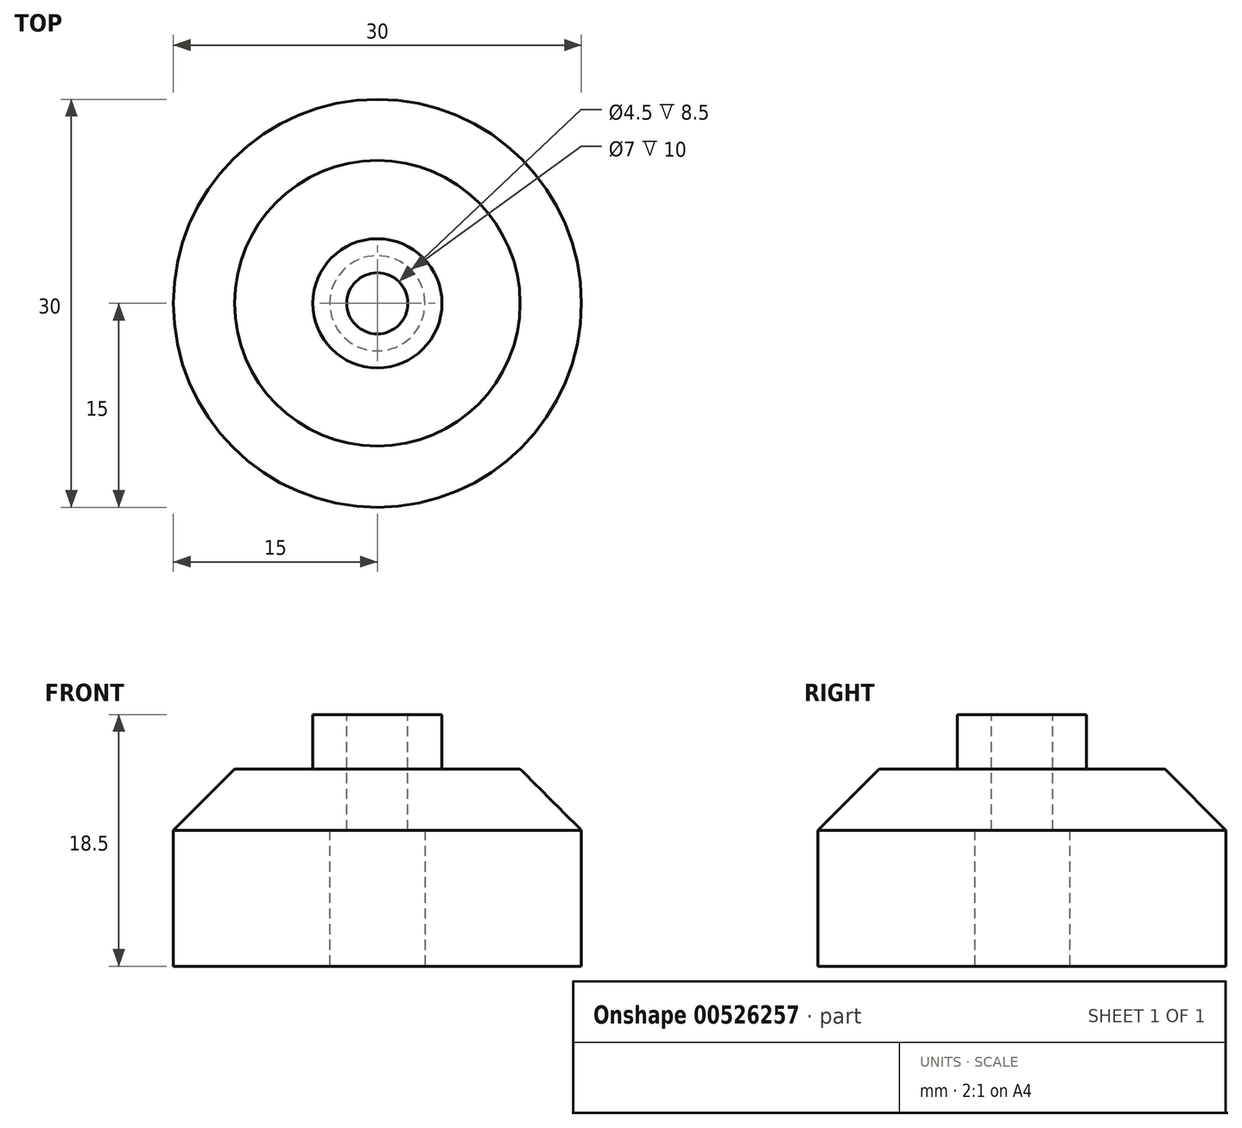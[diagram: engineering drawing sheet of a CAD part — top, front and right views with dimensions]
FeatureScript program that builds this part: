
annotation { "Feature Type Name" : "Feature", "Feature Type Description" : "" }
export const myFeature = defineFeature(function(context is Context, id is Id, definition is map)
    precondition{}
    {
        {
            var Q0;
            Q0=qCreatedBy(makeId("Top.planeOp"),FACE);
            var sketch = newSketch(context, id + "F0", { "sketchPlane" : qUnion([Q0])});
            skCircle(sketch, "E0", {"center": v(0, 0) * mm, "radius": 15 * mm});
            skSolve(sketch);
        }
        {
            var Q0;
            Q0=makeQuery(id+"F0.imprint","IMPRINT",FACE,{"disambiguationData":[TD([[makeQuery(id+"F0.imprint","IMPRINT",EDGE,{"derivedFrom":sQuery(id+"F0.wireOp",EDGE,"E0")}),1.0]])]});
            var Q1;
            Q1=sQuery(id+"F0.wireOp",EDGE,"E0");
            extrude(context, id + "F1", {"entities" : qUnion([Q0]), "surfaceEntities" : qUnion([Q1]), "depth" : 10 * mm, "offsetDistance" : 25.4 * mm});
        }
        {
            var Q0;
            Q0=makeQuery(id+"F1.opExtrude","CAP_FACE",FACE,{"disambiguationData":[OSD([sQuery(id+"F0.wireOp",EDGE,"E0")])],"isStart":false});
            var sketch = newSketch(context, id + "F2", { "sketchPlane" : qUnion([Q0])});
            skSolve(sketch);
        }
        {
            var Q0;
            Q0=makeQuery(id+"F2.imprint","IMPRINT",FACE,{"disambiguationData":[TD([[makeQuery(id+"F2.imprint","IMPRINT",EDGE,{"derivedFrom":makeQuery(id+"F1.opExtrude","CAP_EDGE",EDGE,{"disambiguationData":[OSD([sQuery(id+"F0.wireOp",EDGE,"E0")])],"isStart":false})}),1.0]])]});
            extrude(context, id + "F3", {"entities" : qUnion([Q0]), "operationType" : NewBodyOperationType.ADD, "depth" : 4.5 * mm, "offsetDistance" : 25.4 * mm});
        }
        {
            var Q0;
            Q0=makeQuery(id+"F3.opExtrude","CAP_EDGE",EDGE,{"disambiguationData":[OSD([sQuery(id+"F0.wireOp",EDGE,"E0")])],"isStart":false});
            chamfer(context, id + "F4", {"entities" : qUnion([Q0]), "chamferType" : ChamferType.OFFSET_ANGLE, "width" : 4.5 * mm, "oppositeDirection" : false, "angle" : 45 * degree, "tangentPropagation" : true});
        }
        {
            var Q0;
            Q0=makeQuery(id+"F3.opExtrude","CAP_FACE",FACE,{"disambiguationData":[OSD([sQuery(id+"F0.wireOp",EDGE,"E0")])],"isStart":false});
            var sketch = newSketch(context, id + "F5", { "sketchPlane" : qUnion([Q0])});
            skCircle(sketch, "E1", {"center": v(0, 0) * mm, "radius": 2.25 * mm});
            skSolve(sketch);
        }
        {
            var Q0;
            Q0=makeQuery(id+"F5.imprint","IMPRINT",FACE,{"disambiguationData":[TD([[makeQuery(id+"F5.imprint","IMPRINT",EDGE,{"derivedFrom":sQuery(id+"F5.wireOp",EDGE,"E1")}),1.0]])]});
            extrude(context, id + "F6", {"entities" : qUnion([Q0]), "operationType" : NewBodyOperationType.REMOVE, "oppositeDirection" : true, "depth" : 4.5 * mm, "offsetDistance" : 25.4 * mm});
        }
        {
            var Q0;
            Q0=makeQuery(id+"F0.imprint","IMPRINT",FACE,{"disambiguationData":[TD([[makeQuery(id+"F0.imprint","IMPRINT",EDGE,{"derivedFrom":sQuery(id+"F0.wireOp",EDGE,"E0")}),1.0]])]});
            var sketch = newSketch(context, id + "F7", { "sketchPlane" : qUnion([Q0])});
            skCircle(sketch, "E2", {"center": v(0, 0) * mm, "radius": 3.5 * mm});
            skSolve(sketch);
        }
        {
            var Q0;
            Q0 = qSketchRegion(id + "F7", true);
            extrude(context, id + "F8", {"entities" : qUnion([Q0]), "operationType" : NewBodyOperationType.REMOVE, "depth" : 10 * mm, "offsetDistance" : 25.4 * mm});
        }
        {
            var Q0;
            Q0=makeQuery(id+"F3.opExtrude","CAP_FACE",FACE,{"disambiguationData":[OSD([sQuery(id+"F0.wireOp",EDGE,"E0")])],"isStart":false});
            var sketch = newSketch(context, id + "F9", { "sketchPlane" : qUnion([Q0])});
            skCircle(sketch, "E3", {"center": v(0, 0) * mm, "radius": 4.75 * mm});
            skSolve(sketch);
        }
        {
            var Q0;
            Q0=makeQuery(id+"F9.imprint","IMPRINT",FACE,{"disambiguationData":[TD([[makeQuery(id+"F9.imprint","IMPRINT",EDGE,{"derivedFrom":sQuery(id+"F9.wireOp",EDGE,"E3")}),1.0]])]});
            var Q1;
            Q1=sQuery(id+"F9.wireOp",EDGE,"E3");
            extrude(context, id + "F10", {"entities" : qUnion([Q0]), "operationType" : NewBodyOperationType.ADD, "surfaceEntities" : qUnion([Q1]), "depth" : 4 * mm, "offsetDistance" : 25.4 * mm});
        }
    });
